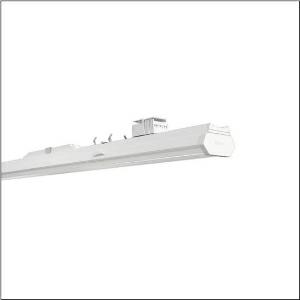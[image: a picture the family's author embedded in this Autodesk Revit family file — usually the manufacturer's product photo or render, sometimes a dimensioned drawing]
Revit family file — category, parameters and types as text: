
# Revit family: licross_r__11_protected_ho_51tp13cn4e5s_b79e
name_source: partatom
category: Lighting Fixtures
units: mm (PartAtom-declared; Revit-internal decimal feet)

## family parameters
Cut with Voids When Loaded = No
Host = Face
Light Source = No
Part Type = Normal
Room Calculation Point = No
Round Connector Dimension = Use Diameter
Shared = No

## types (1)
- --- (1 x LED, 14500 lm, 77.6 W, 4000K)
    Apparent Load = 78 VA
    CIE Flux Codes = 89 96 99 100 99
    Color Rendering = 80
    Color Temperature = 4000K
    Default Elevation = 1800 mm
    Description = Licross® 11 Protected HO, luminaire insert, of sheet steel, galvanised, coil coated, white, length: 1.500mm, width: 90mm, height: 101mm, LED rated luminous flux: 14.500lm, light colour: 840, control gear: ON/OFF Multilumen, CLOi, with plug, 3-pole, with phase selection, mains connection: 220..240V, AC, 50/60Hz, halogen-free wiring, primary light control with lens, of plastic, primary optical cover: cover, of PMMA, light emission: direct with ceiling illumination distribution, primary light characteristic: symmetric, protection rating (complete): IP64, insulation class (complete): insulation class I (protective earthing), certification: CE, ENEC, VDE, UKCA, protection symbol: D if used in an environment with conductive dust loads with corresponding accessories, impact resistance: IK06, permissible ambient temperature for indoor applications: -35..+35°C, corresponds to IFS (International Featured Standards) requirements for safety and quality in the food industry, reducing of maximum allowable ambient temperature of 5°C with ceiling mounting, LABS conformity tested according to VDMA 24364:2018-05, packaging unit: 1 piece
    Height = 92 mm
    Lamp = 1 x LED
    Lamp Light Flux = 14500 lm
    Lamp Power = 77.6 W
    Lamp count = 1
    Length = 1500 mm
    Luminous efficacy = 187 lm/W
    Manufacturer = Siteco
    ModVariant = No
    Model = 51TP13CN4E5S
    Mounting Place = Ceiling
    Mounting Type = Pendant
    Number of Poles = 1
    OnlyDefault = Yes
    Power Factor = 1
    Product Name = Licross® 11 Protected HO
    Product group = luminaire insert
    ProductGroupID = 902
    Protection Class = Protection class I
    Protection Degree = IP 64
    RLX_Detail_Level = 1
    RlxData = <blob elided: 22085 chars, md5=b3d77970>
    Socket = socket
    Standby Power = 0 W
    System Light Flux = 14500 lm
    System Power = 78 W
    Type Comments = factory setting: luminous flux: 100 % | (A | C | E) | 181 mA
    Type Image = l_1256148.jpg
    URL = http://relux.com
    VarID = @adj_003623
    Voltage = 0 V
    Weight = 0.00 kg
    Width = 88 mm

## geometry (parser evidence)
native form markers: Blend x4, Sweep x11
no freeform markers — native parametric forms only
